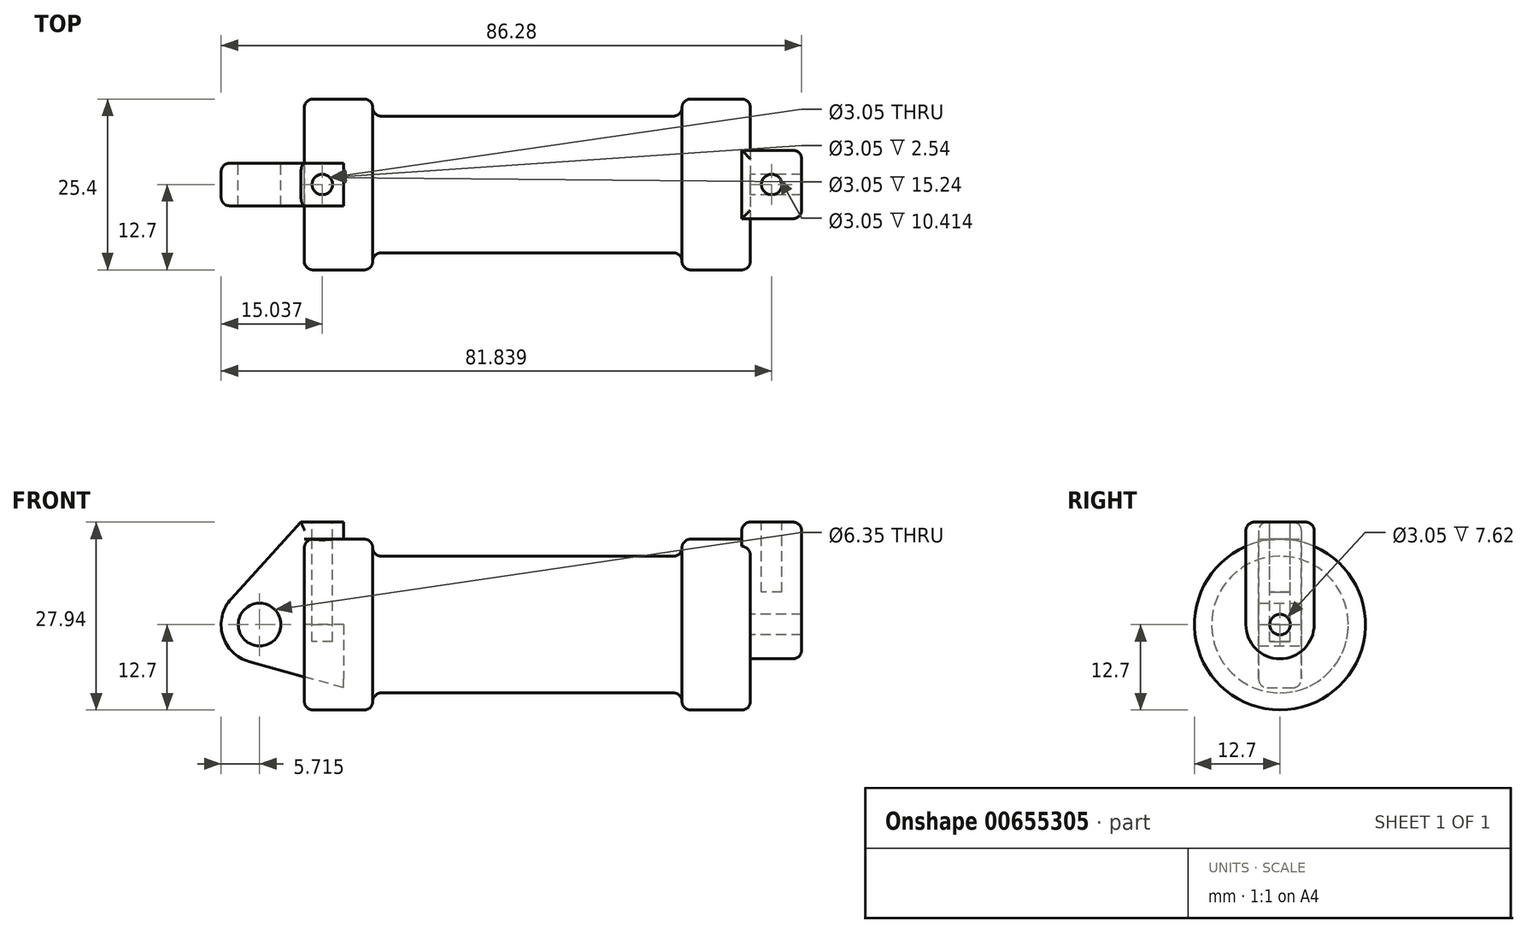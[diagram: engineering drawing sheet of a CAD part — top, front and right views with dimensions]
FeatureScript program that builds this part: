
annotation { "Feature Type Name" : "Feature", "Feature Type Description" : "" }
export const myFeature = defineFeature(function(context is Context, id is Id, definition is map)
    precondition{}
    {
        {
            var Q0;
            Q0=qCreatedBy(makeId("Front.planeOp"),FACE);
            var sketch = newSketch(context, id + "F0", { "sketchPlane" : qUnion([Q0])});
            skLineSegment(sketch, "E0", {"start": v(0, 0) * mm, "end": v(0, 12.7) * mm});
            skLineSegment(sketch, "E1", {"start": v(0, 12.7) * mm, "end": v(10.16, 12.7) * mm});
            skLineSegment(sketch, "E2", {"start": v(10.16, 12.7) * mm, "end": v(10.16, 10.16) * mm});
            skLineSegment(sketch, "E3", {"start": v(10.16, 10.16) * mm, "end": v(56.13, 10.16) * mm});
            skLineSegment(sketch, "E4", {"start": v(56.13, 10.16) * mm, "end": v(56.13, 12.7) * mm});
            skLineSegment(sketch, "E5", {"start": v(56.13, 12.7) * mm, "end": v(66.3, 12.7) * mm});
            skLineSegment(sketch, "E6", {"start": v(66.3, 12.7) * mm, "end": v(66.3, 0) * mm});
            skLineSegment(sketch, "E7", {"start": v(66.3, 0) * mm, "end": v(0, 0) * mm});
            skLineSegment(sketch, "E8", {"start": v(5.84, 15.24) * mm, "end": v(-0.5, 15.24) * mm});
            skLineSegment(sketch, "E9", {"start": v(-0.5, 15.24) * mm, "end": v(-10.88, 3.85) * mm});
            skLineSegment(sketch, "E10", {"start": v(0, 0) * mm, "end": v(-6.65, 0) * mm});
            skCircle(sketch, "E11", {"center": v(-6.65, 0) * mm, "radius": 5.72 * mm});
            skCircle(sketch, "E12", {"center": v(-6.65, 0) * mm, "radius": 3.18 * mm});
            skLineSegment(sketch, "E13", {"start": v(5.84, 15.24) * mm, "end": v(5.84, -9.4) * mm});
            skLineSegment(sketch, "E14", {"start": v(5.84, -9.4) * mm, "end": v(-8.18, -5.5) * mm});
            skSolve(sketch);
        }
        {
            var Q0;
            {var subQ0=sQuery(id+"F0.wireOp",EDGE,"E0");Q0=makeQuery(id+"F0.imprint","IMPRINT",FACE,{"disambiguationData":[TD([[makeQuery(id+"F0.imprint","IMPRINT",EDGE,{"derivedFrom":subQ0}),-1.0]])]});}
            var Q1;
            {var subQ0=sQuery(id+"F0.wireOp",EDGE,"E2");Q1=makeQuery(id+"F0.imprint","IMPRINT",FACE,{"disambiguationData":[TD([[makeQuery(id+"F0.imprint","IMPRINT",EDGE,{"derivedFrom":subQ0}),-1.0]])]});}
            var Q2;
            Q2=sQuery(id+"F0.wireOp",EDGE,"E7");
            revolve(context, id + "F1", {"entities" : qUnion([Q0, Q1]), "axis" : qUnion([Q2]), "revolveType" : RevolveType.FULL});
        }
        {
            var Q0;
            {var subQ1=sQuery(id+"F0.wireOp",EDGE,"E0");Q0=makeQuery(id+"F0.imprint","IMPRINT",FACE,{"disambiguationData":[TD([[makeQuery(id+"F0.imprint","IMPRINT",EDGE,{"derivedFrom":subQ1}),1.0]])]});}
            var Q1;
            {var subQ5=sQuery(id+"F0.wireOp",EDGE,"E12");Q1=makeQuery(id+"F0.imprint","IMPRINT",FACE,{"disambiguationData":[TD([[makeQuery(id+"F0.imprint","IMPRINT",EDGE,{"derivedFrom":subQ5}),-1.0]])]});}
            var Q2;
            {var subQ0=sQuery(id+"F0.wireOp",EDGE,"E14");Q2=makeQuery(id+"F0.imprint","IMPRINT",FACE,{"disambiguationData":[TD([[makeQuery(id+"F0.imprint","IMPRINT",EDGE,{"derivedFrom":subQ0}),-1.0]])]});}
            extrude(context, id + "F2", {"entities" : qUnion([Q0, Q1, Q2]), "endBound" : BoundingType.SYMMETRIC, "depth" : 6.35 * mm, "offsetDistance" : 25.4 * mm});
        }
        {
            var Q0;
            Q0=makeQuery(id+"F1.opRevolve","SWEPT_FACE",FACE,{"disambiguationData":[OSD([sQuery(id+"F0.wireOp",EDGE,"E6")])]});
            var sketch = newSketch(context, id + "F3", { "sketchPlane" : qUnion([Q0])});
            skCircle(sketch, "E15", {"center": v(0, 0) * mm, "radius": 5.08 * mm});
            skCircle(sketch, "E16", {"center": v(0, 0) * mm, "radius": 1.52 * mm});
            skLineSegment(sketch, "E17", {"start": v(-5.08, 0) * mm, "end": v(-5.08, 15.24) * mm});
            skLineSegment(sketch, "E18", {"start": v(-5.08, 15.24) * mm, "end": v(5.08, 15.24) * mm});
            skLineSegment(sketch, "E19", {"start": v(5.08, 15.24) * mm, "end": v(5.08, 0) * mm});
            skSolve(sketch);
        }
        {
            var Q0;
            Q0=makeQuery(id+"F3.imprint","IMPRINT",FACE,{"disambiguationData":[TD([[makeQuery(id+"F3.imprint","IMPRINT",EDGE,{"derivedFrom":sQuery(id+"F3.wireOp",EDGE,"E16")}),-1.0]])]});
            var Q1;
            {var subQ0=sQuery(id+"F3.wireOp",EDGE,"E17");var subQ1=sQuery(id+"F3.wireOp",EDGE,"E15");var subQ2=makeQuery(id+"F3.imprint","INTERSECT",VERTEX,{"derivedFrom":[subQ1,subQ0]});Q1=makeQuery(id+"F3.imprint","IMPRINT",FACE,{"disambiguationData":[TD([[makeQuery(id+"F3.imprint","IMPRINT",EDGE,{"disambiguationData":[TD([[subQ2,1.0]])],"derivedFrom":subQ1}),-1.0]])]});}
            var Q2;
            {var subQ0=sQuery(id+"F3.wireOp",EDGE,"E18");Q2=makeQuery(id+"F3.imprint","IMPRINT",FACE,{"disambiguationData":[TD([[makeQuery(id+"F3.imprint","IMPRINT",EDGE,{"derivedFrom":subQ0}),-1.0]])]});}
            extrude(context, id + "F4", {"entities" : qUnion([Q0, Q1, Q2]), "operationType" : NewBodyOperationType.ADD, "depth" : 7.62 * mm, "offsetDistance" : 25.4 * mm, "hasSecondDirection" : true, "secondDirectionOppositeDirection" : true, "secondDirectionDepth" : 1.27 * mm});
        }
        {
            var Q0;
            Q0=makeQuery(id+"F4.opExtrude","SWEPT_FACE",FACE,{"disambiguationData":[OSD([sQuery(id+"F3.wireOp",EDGE,"E18")])]});
            var sketch = newSketch(context, id + "F5", { "sketchPlane" : qUnion([Q0])});
            skCircle(sketch, "E20", {"center": v(69.47, 0) * mm, "radius": 1.52 * mm});
            skPoint(sketch, "E20.centerSnap0", {"position": v(73.91, 0) * mm});
            skPoint(sketch, "E20.centerSnap1", {"position": v(69.47, -5.08) * mm});
            skSolve(sketch);
        }
        {
            var Q0;
            Q0=makeQuery(id+"F2.opExtrude","SWEPT_FACE",FACE,{"disambiguationData":[OSD([sQuery(id+"F0.wireOp",EDGE,"E8")])]});
            var sketch = newSketch(context, id + "F6", { "sketchPlane" : qUnion([Q0])});
            skCircle(sketch, "E21", {"center": v(2.67, 0) * mm, "radius": 1.52 * mm});
            skPoint(sketch, "E21.centerSnap0", {"position": v(5.84, 0) * mm});
            skPoint(sketch, "E21.centerSnap1", {"position": v(2.67, 3.18) * mm});
            skSolve(sketch);
        }
        {
            var Q0;
            Q0=makeQuery(id+"F6.imprint","IMPRINT",FACE,{"disambiguationData":[TD([[makeQuery(id+"F6.imprint","IMPRINT",EDGE,{"derivedFrom":sQuery(id+"F6.wireOp",EDGE,"E21")}),1.0]])]});
            extrude(context, id + "F7", {"entities" : qUnion([Q0]), "operationType" : NewBodyOperationType.REMOVE, "oppositeDirection" : true, "depth" : 17.78 * mm, "offsetDistance" : 25.4 * mm});
        }
        {
            var Q0;
            Q0=makeQuery(id+"F5.imprint","IMPRINT",FACE,{"disambiguationData":[TD([[makeQuery(id+"F5.imprint","IMPRINT",EDGE,{"derivedFrom":sQuery(id+"F5.wireOp",EDGE,"E20")}),1.0]])]});
            var Q1;
            Q1=sQuery(id+"F5.wireOp",EDGE,"E20");
            extrude(context, id + "F8", {"entities" : qUnion([Q0]), "operationType" : NewBodyOperationType.REMOVE, "surfaceEntities" : qUnion([Q1]), "oppositeDirection" : true, "depth" : 10.4 * mm, "offsetDistance" : 25.4 * mm});
        }
        {
            var Q0;
            Q0=makeQuery(id+"F1.opRevolve","SWEPT_EDGE",EDGE,{"disambiguationData":[OSD([sQuery(id+"F0.wireOp",EDGE,"E0"),sQuery(id+"F0.wireOp",EDGE,"E1")])]});
            var Q1;
            Q1=makeQuery(id+"F1.opRevolve","SWEPT_EDGE",EDGE,{"disambiguationData":[OSD([sQuery(id+"F0.wireOp",EDGE,"E1"),sQuery(id+"F0.wireOp",EDGE,"E2")])]});
            var Q2;
            Q2=makeQuery(id+"F1.opRevolve","SWEPT_EDGE",EDGE,{"disambiguationData":[OSD([sQuery(id+"F0.wireOp",EDGE,"E4"),sQuery(id+"F0.wireOp",EDGE,"E5")])]});
            var Q3;
            Q3=makeQuery(id+"F1.opRevolve","SWEPT_EDGE",EDGE,{"disambiguationData":[OSD([sQuery(id+"F0.wireOp",EDGE,"E5"),sQuery(id+"F0.wireOp",EDGE,"E6")])]});
            var Q4;
            Q4=makeQuery(id+"F1.opRevolve","SWEPT_EDGE",EDGE,{"disambiguationData":[OSD([sQuery(id+"F0.wireOp",EDGE,"E2"),sQuery(id+"F0.wireOp",EDGE,"E3")])]});
            var Q5;
            Q5=makeQuery(id+"F1.opRevolve","SWEPT_EDGE",EDGE,{"disambiguationData":[OSD([sQuery(id+"F0.wireOp",EDGE,"E3"),sQuery(id+"F0.wireOp",EDGE,"E4")])]});
            fillet(context, id + "F9", {"entities" : qUnion([Q0, Q1, Q2, Q3, Q4, Q5]), "radius" : 1.27 * mm, "tangentPropagation" : true, "allowEdgeOverflow" : false});
        }
        {
            var Q0;
            Q0=makeQuery(id+"F2.opExtrude","CAP_EDGE",EDGE,{"disambiguationData":[OSD([sQuery(id+"F0.wireOp",EDGE,"E8")])],"isStart":false});
            var Q1;
            Q1=makeQuery(id+"F2.opExtrude","CAP_EDGE",EDGE,{"disambiguationData":[OSD([sQuery(id+"F0.wireOp",EDGE,"E9")])],"isStart":false});
            var Q2;
            Q2=makeQuery(id+"F2.opExtrude","CAP_EDGE",EDGE,{"disambiguationData":[OSD([sQuery(id+"F0.wireOp",EDGE,"E8")])],"isStart":true});
            var Q3;
            Q3=makeQuery(id+"F2.opExtrude","CAP_EDGE",EDGE,{"disambiguationData":[OSD([sQuery(id+"F0.wireOp",EDGE,"E9")])],"isStart":true});
            var Q4;
            Q4=makeQuery(id+"F2.opExtrude","CAP_EDGE",EDGE,{"disambiguationData":[OSD([sQuery(id+"F0.wireOp",EDGE,"E11")])],"isStart":true});
            fillet(context, id + "F10", {"entities" : qUnion([Q0, Q1, Q2, Q3, Q4]), "radius" : 1.27 * mm, "tangentPropagation" : true, "allowEdgeOverflow" : false});
        }
        {
            var Q0;
            Q0=makeQuery(id+"F4.opExtrude","SWEPT_EDGE",EDGE,{"disambiguationData":[OSD([sQuery(id+"F3.wireOp",EDGE,"E17"),sQuery(id+"F3.wireOp",EDGE,"E18")])]});
            var Q1;
            Q1=makeQuery(id+"F4.opExtrude","CAP_EDGE",EDGE,{"disambiguationData":[OSD([sQuery(id+"F3.wireOp",EDGE,"E18")])],"isStart":false});
            var Q2;
            Q2=makeQuery(id+"F4.opExtrude","SWEPT_EDGE",EDGE,{"disambiguationData":[OSD([sQuery(id+"F3.wireOp",EDGE,"E18"),sQuery(id+"F3.wireOp",EDGE,"E19")])]});
            var Q3;
            Q3=makeQuery(id+"F4.opExtrude","CAP_EDGE",EDGE,{"disambiguationData":[OSD([sQuery(id+"F3.wireOp",EDGE,"E19")])],"isStart":false});
            var Q4;
            Q4=makeQuery(id+"F4.opExtrude","CAP_EDGE",EDGE,{"disambiguationData":[OSD([sQuery(id+"F3.wireOp",EDGE,"E17")])],"isStart":false});
            var Q5;
            Q5=makeQuery(id+"F4.opExtrude","CAP_EDGE",EDGE,{"disambiguationData":[OSD([sQuery(id+"F3.wireOp",EDGE,"E18")])],"isStart":true});
            fillet(context, id + "F11", {"entities" : qUnion([Q0, Q1, Q2, Q3, Q4, Q5]), "radius" : 1.27 * mm, "tangentPropagation" : true, "allowEdgeOverflow" : false});
        }
    });
